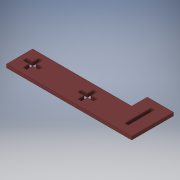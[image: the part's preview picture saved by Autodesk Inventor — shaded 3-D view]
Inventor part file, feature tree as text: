
AUTODESK INVENTOR PART (.ipt)
format: ipt  version: 2019 (Build 230136000, 136)  size: 158,208 bytes
history: native  units: mm
features: extrude x1, sketch x1
ambient origin geometry x8: Origin, YZ Plane, XZ Plane, XY Plane, X Axis, Y Axis, Z Axis, Center Point
bodies: Body1 (feature_tree)
feature tree (2):
  extrude  "Extrusion2"  Depth=25.0mm
  sketch  "Sketch1"  dims[d0=3.18mm d1=25.0mm d2=25.0mm d3=12.5mm d4=20.0mm d5=20.0mm d6=95.0mm d7=25.0mm d35=15.0mm d36=3.18mm d38=3.18mm d39=15.0mm d40=7.5mm d41=1.59mm d42=12.5mm d43=12.5mm d44=15.0mm d45=3.18mm d46=3.18mm d47=15.0mm d48=7.5mm d49=1.59mm d50=30.0mm d51=12.5mm d52=3.18mm d53=0.0mm]
